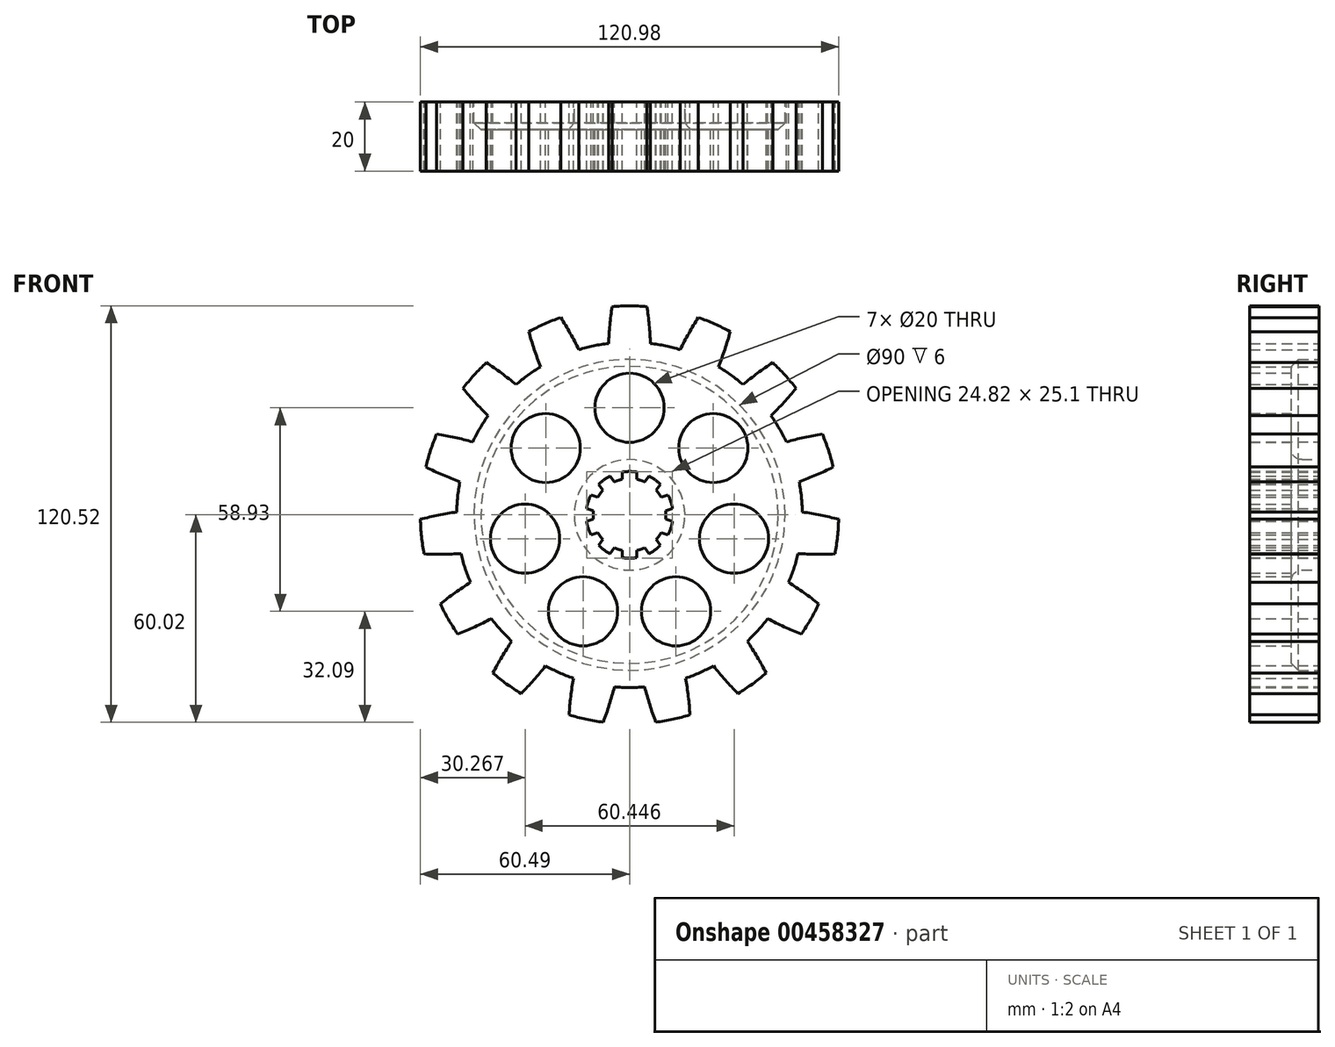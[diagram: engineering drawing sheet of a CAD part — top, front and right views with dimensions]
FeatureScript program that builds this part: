
annotation { "Feature Type Name" : "Feature", "Feature Type Description" : "" }
export const myFeature = defineFeature(function(context is Context, id is Id, definition is map)
    precondition{}
    {
        {
            var Q0;
            Q0=qCreatedBy(makeId("Front.planeOp"),FACE);
            var sketch = newSketch(context, id + "F0", { "sketchPlane" : qUnion([Q0])});
            skCircle(sketch, "E0", {"center": v(0, 0) * mm, "radius": 10.5 * mm});
            skSolve(sketch);
        }
        {
            var Q0;
            Q0=qCreatedBy(makeId("Front.planeOp"),FACE);
            var sketch = newSketch(context, id + "F1", { "sketchPlane" : qUnion([Q0])});
            skArc(sketch, "E1", {"start": v(2.05, 12.38) * mm, "mid": v(0, 12.55) * mm, "end": v(-2.05, 12.38) * mm});
            skLineSegment(sketch, "E2", {"start": v(-2.05, 6.3) * mm, "end": v(-2.05, -6.3) * mm});
            skLineSegment(sketch, "E3", {"start": v(2.05, 6.3) * mm, "end": v(2.05, -6.3) * mm});
            skLineSegment(sketch, "E4", {"start": v(2.05, -14.67) * mm, "end": v(-2.05, -14.67) * mm});
            skArc(sketch, "E5.trimOffspring", {"start": v(-2.05, -12.38) * mm, "mid": v(0, -12.55) * mm, "end": v(2.05, -12.38) * mm});
            skPoint(sketch, "E6.orphan", {"position": v(-2.05, 16.5) * mm});
            skPoint(sketch, "E7.orphan", {"position": v(2.05, 16.45) * mm});
            skLineSegment(sketch, "E8.1.0", {"start": v(-8.94, 8.81) * mm, "end": v(-7.71, 7.13) * mm});
            skArc(sketch, "E8.1.1", {"start": v(-5.62, 11.22) * mm, "mid": v(-7.38, 10.15) * mm, "end": v(-8.94, 8.81) * mm});
            skLineSegment(sketch, "E8.1.2", {"start": v(-5.62, 11.22) * mm, "end": v(-4.4, 9.54) * mm});
            skArc(sketch, "E8.1.3", {"start": v(5.62, -11.22) * mm, "mid": v(7.38, -10.15) * mm, "end": v(8.94, -8.81) * mm});
            skLineSegment(sketch, "E8.2.0", {"start": v(-12.4, 1.88) * mm, "end": v(-10.43, 1.23) * mm});
            skArc(sketch, "E8.2.1", {"start": v(-11.14, 5.78) * mm, "mid": v(-11.94, 3.88) * mm, "end": v(-12.4, 1.88) * mm});
            skLineSegment(sketch, "E8.2.2", {"start": v(-11.14, 5.78) * mm, "end": v(-9.16, 5.13) * mm});
            skArc(sketch, "E8.2.3", {"start": v(11.14, -5.78) * mm, "mid": v(11.94, -3.88) * mm, "end": v(12.4, -1.88) * mm});
            skLineSegment(sketch, "E8.3.0", {"start": v(-11.14, -5.78) * mm, "end": v(-9.16, -5.13) * mm});
            skArc(sketch, "E8.3.1", {"start": v(-12.4, -1.88) * mm, "mid": v(-11.94, -3.88) * mm, "end": v(-11.14, -5.78) * mm});
            skLineSegment(sketch, "E8.3.2", {"start": v(-12.4, -1.88) * mm, "end": v(-10.43, -1.23) * mm});
            skArc(sketch, "E8.3.3", {"start": v(12.4, 1.88) * mm, "mid": v(11.94, 3.88) * mm, "end": v(11.14, 5.78) * mm});
            skLineSegment(sketch, "E8.4.0", {"start": v(-5.62, -11.22) * mm, "end": v(-4.4, -9.54) * mm});
            skArc(sketch, "E8.4.1", {"start": v(-8.94, -8.81) * mm, "mid": v(-7.38, -10.15) * mm, "end": v(-5.62, -11.22) * mm});
            skLineSegment(sketch, "E8.4.2", {"start": v(-8.94, -8.81) * mm, "end": v(-7.71, -7.13) * mm});
            skArc(sketch, "E8.4.3", {"start": v(8.94, 8.81) * mm, "mid": v(7.38, 10.15) * mm, "end": v(5.62, 11.22) * mm});
            skLineSegment(sketch, "E8.5.0", {"start": v(2.05, -12.38) * mm, "end": v(2.05, -10.3) * mm});
            skLineSegment(sketch, "E8.5.2", {"start": v(-2.05, -12.38) * mm, "end": v(-2.05, -10.3) * mm});
            skLineSegment(sketch, "E8.6.0", {"start": v(8.94, -8.81) * mm, "end": v(7.71, -7.13) * mm});
            skArc(sketch, "E8.6.1", {"start": v(5.62, -11.22) * mm, "mid": v(7.38, -10.15) * mm, "end": v(8.94, -8.81) * mm});
            skLineSegment(sketch, "E8.6.2", {"start": v(5.62, -11.22) * mm, "end": v(4.4, -9.54) * mm});
            skArc(sketch, "E8.6.3", {"start": v(-5.62, 11.22) * mm, "mid": v(-7.38, 10.15) * mm, "end": v(-8.94, 8.81) * mm});
            skLineSegment(sketch, "E8.7.0", {"start": v(12.4, -1.88) * mm, "end": v(10.43, -1.23) * mm});
            skArc(sketch, "E8.7.1", {"start": v(11.14, -5.78) * mm, "mid": v(11.94, -3.88) * mm, "end": v(12.4, -1.88) * mm});
            skLineSegment(sketch, "E8.7.2", {"start": v(11.14, -5.78) * mm, "end": v(9.16, -5.13) * mm});
            skArc(sketch, "E8.7.3", {"start": v(-11.14, 5.78) * mm, "mid": v(-11.94, 3.88) * mm, "end": v(-12.4, 1.88) * mm});
            skLineSegment(sketch, "E8.8.0", {"start": v(11.14, 5.78) * mm, "end": v(9.16, 5.13) * mm});
            skArc(sketch, "E8.8.1", {"start": v(12.4, 1.88) * mm, "mid": v(11.94, 3.88) * mm, "end": v(11.14, 5.78) * mm});
            skLineSegment(sketch, "E8.8.2", {"start": v(12.4, 1.88) * mm, "end": v(10.43, 1.23) * mm});
            skArc(sketch, "E8.8.3", {"start": v(-12.4, -1.88) * mm, "mid": v(-11.94, -3.88) * mm, "end": v(-11.14, -5.78) * mm});
            skLineSegment(sketch, "E8.9.0", {"start": v(5.62, 11.22) * mm, "end": v(4.4, 9.54) * mm});
            skArc(sketch, "E8.9.1", {"start": v(8.94, 8.81) * mm, "mid": v(7.38, 10.15) * mm, "end": v(5.62, 11.22) * mm});
            skLineSegment(sketch, "E8.9.2", {"start": v(8.94, 8.81) * mm, "end": v(7.71, 7.13) * mm});
            skArc(sketch, "E8.9.3", {"start": v(-8.94, -8.81) * mm, "mid": v(-7.38, -10.15) * mm, "end": v(-5.62, -11.22) * mm});
            skCircle(sketch, "E9", {"center": v(0, 0) * mm, "radius": 50 * mm});
            skCircle(sketch, "E10", {"center": v(0, 0) * mm, "radius": 10.5 * mm});
            skLineSegment(sketch, "E11.trimOffspring", {"start": v(-2.05, 10.3) * mm, "end": v(-2.05, 12.38) * mm});
            skLineSegment(sketch, "E12.trimOffspring", {"start": v(-2.05, 6.3) * mm, "end": v(5.37, -3.9) * mm});
            skLineSegment(sketch, "E13.trimOffspring", {"start": v(-5.37, 3.9) * mm, "end": v(2.05, -6.3) * mm});
            skLineSegment(sketch, "E14.trimOffspring", {"start": v(-5.37, 3.9) * mm, "end": v(6.63, 0) * mm});
            skLineSegment(sketch, "E15.trimOffspring", {"start": v(-9.16, 5.13) * mm, "end": v(-11.14, 5.78) * mm});
            skLineSegment(sketch, "E16.trimOffspring", {"start": v(-6.63, 0) * mm, "end": v(5.37, -3.9) * mm});
            skLineSegment(sketch, "E17.trimOffspring", {"start": v(-10.43, -1.23) * mm, "end": v(-12.4, -1.88) * mm});
            skLineSegment(sketch, "E18.trimOffspring", {"start": v(-9.16, -5.13) * mm, "end": v(-11.14, -5.78) * mm});
            skLineSegment(sketch, "E19.trimOffspring", {"start": v(-6.63, 0) * mm, "end": v(5.37, 3.9) * mm});
            skLineSegment(sketch, "E20.trimOffspring", {"start": v(-10.43, 1.23) * mm, "end": v(-12.4, 1.88) * mm});
            skLineSegment(sketch, "E21.trimOffspring", {"start": v(-5.37, -3.9) * mm, "end": v(2.05, 6.3) * mm});
            skLineSegment(sketch, "E22.trimOffspring", {"start": v(-7.71, -7.13) * mm, "end": v(-8.94, -8.81) * mm});
            skLineSegment(sketch, "E23.trimOffspring", {"start": v(-5.37, -3.9) * mm, "end": v(6.63, 0) * mm});
            skLineSegment(sketch, "E24.trimOffspring", {"start": v(-2.05, -6.3) * mm, "end": v(5.37, 3.9) * mm});
            skLineSegment(sketch, "E25.trimOffspring", {"start": v(-2.05, -10.3) * mm, "end": v(-2.05, -12.38) * mm});
            skLineSegment(sketch, "E26.trimOffspring", {"start": v(-4.4, -9.54) * mm, "end": v(-5.62, -11.22) * mm});
            skLineSegment(sketch, "E27.trimOffspring", {"start": v(-2.05, -6.3) * mm, "end": v(-2.05, 6.3) * mm});
            skLineSegment(sketch, "E28.trimOffspring", {"start": v(2.05, -10.3) * mm, "end": v(2.05, -12.38) * mm});
            skLineSegment(sketch, "E29.trimOffspring", {"start": v(2.05, -6.3) * mm, "end": v(2.05, 2.82) * mm});
            skLineSegment(sketch, "E30.trimOffspring", {"start": v(4.4, -9.54) * mm, "end": v(5.62, -11.22) * mm});
            skLineSegment(sketch, "E31.trimOffspring", {"start": v(2.05, -6.3) * mm, "end": v(-8.94, 8.81) * mm});
            skLineSegment(sketch, "E32.trimOffspring", {"start": v(5.37, -3.9) * mm, "end": v(-2.05, 6.3) * mm});
            skLineSegment(sketch, "E33.trimOffspring", {"start": v(7.71, -7.13) * mm, "end": v(8.94, -8.81) * mm});
            skLineSegment(sketch, "E34.trimOffspring", {"start": v(9.16, -5.13) * mm, "end": v(11.14, -5.78) * mm});
            skLineSegment(sketch, "E35.trimOffspring", {"start": v(5.37, -3.9) * mm, "end": v(-6.63, 0) * mm});
            skLineSegment(sketch, "E36.trimOffspring", {"start": v(10.43, -1.23) * mm, "end": v(12.4, -1.88) * mm});
            skLineSegment(sketch, "E37.trimOffspring", {"start": v(6.63, 0) * mm, "end": v(-5.37, 3.9) * mm});
            skLineSegment(sketch, "E38.trimOffspring", {"start": v(6.63, 0) * mm, "end": v(-5.37, -3.9) * mm});
            skLineSegment(sketch, "E39.trimOffspring", {"start": v(10.43, 1.23) * mm, "end": v(12.4, 1.88) * mm});
            skLineSegment(sketch, "E40.trimOffspring", {"start": v(9.16, 5.13) * mm, "end": v(11.14, 5.78) * mm});
            skLineSegment(sketch, "E41.trimOffspring", {"start": v(5.37, 3.9) * mm, "end": v(-6.63, 0) * mm});
            skLineSegment(sketch, "E42.trimOffspring", {"start": v(7.71, 7.13) * mm, "end": v(8.94, 8.81) * mm});
            skLineSegment(sketch, "E43.trimOffspring", {"start": v(2.05, 6.3) * mm, "end": v(-5.37, -3.9) * mm});
            skLineSegment(sketch, "E44.trimOffspring", {"start": v(4.4, 9.54) * mm, "end": v(5.62, 11.22) * mm});
            skLineSegment(sketch, "E45.trimOffspring", {"start": v(5.37, 3.9) * mm, "end": v(-2.05, -6.3) * mm});
            skLineSegment(sketch, "E46.trimOffspring", {"start": v(2.05, 10.3) * mm, "end": v(2.05, 12.38) * mm});
            skSolve(sketch);
        }
        {
            var Q0;
            {var subQ6=sQuery(id+"F1.wireOp",EDGE,"E8.1.2");Q0=makeQuery(id+"F1.imprint","IMPRINT",FACE,{"disambiguationData":[TD([[makeQuery(id+"F1.imprint","IMPRINT",EDGE,{"derivedFrom":subQ6}),1.0]])]});}
            extrude(context, id + "F2", {"entities" : qUnion([Q0]), "depth" : 20 * mm, "offsetDistance" : 25 * mm});
        }
        {
            var Q0;
            Q0=qCreatedBy(makeId("Front.planeOp"),FACE);
            var sketch = newSketch(context, id + "F3", { "sketchPlane" : qUnion([Q0])});
            skArc(sketch, "E47", {"start": v(5.04, 60.29) * mm, "mid": v(0, 60.5) * mm, "end": v(-5.04, 60.29) * mm});
            skLineSegment(sketch, "E48", {"start": v(83.9, 39.47) * mm, "end": v(83.9, 58.43) * mm, "construction": true});
            skLineSegment(sketch, "E49", {"start": v(-3.15, 46.5) * mm, "end": v(91.22, 46.5) * mm, "construction": true});
            skArc(sketch, "E50", {"start": v(-5.04, 60.29) * mm, "mid": v(-5.7, 54.98) * mm, "end": v(-6.05, 49.63) * mm});
            skCircle(sketch, "E51", {"center": v(0, 0) * mm, "radius": 50 * mm});
            skArc(sketch, "E52.MirrorCS", {"start": v(5.04, 60.29) * mm, "mid": v(5.7, 54.98) * mm, "end": v(6.05, 49.63) * mm});
            skArc(sketch, "E53.1.0", {"start": v(-19.92, 57.13) * mm, "mid": v(-24.6, 55.27) * mm, "end": v(-29.12, 53.03) * mm});
            skArc(sketch, "E53.1.1", {"start": v(-29.12, 53.03) * mm, "mid": v(-27.57, 47.9) * mm, "end": v(-25.71, 42.88) * mm});
            skArc(sketch, "E53.1.2", {"start": v(-19.92, 57.13) * mm, "mid": v(-17.15, 52.54) * mm, "end": v(-14.66, 47.8) * mm});
            skArc(sketch, "E53.2.0", {"start": v(-41.43, 44.09) * mm, "mid": v(-44.96, 40.48) * mm, "end": v(-48.17, 36.6) * mm});
            skArc(sketch, "E53.2.1", {"start": v(-48.17, 36.6) * mm, "mid": v(-44.67, 32.55) * mm, "end": v(-40.93, 28.72) * mm});
            skArc(sketch, "E53.2.2", {"start": v(-41.43, 44.09) * mm, "mid": v(-37.04, 41.02) * mm, "end": v(-32.84, 37.7) * mm});
            skArc(sketch, "E53.3.0", {"start": v(-55.78, 23.42) * mm, "mid": v(-57.54, 18.7) * mm, "end": v(-58.9, 13.84) * mm});
            skArc(sketch, "E53.3.1", {"start": v(-58.9, 13.84) * mm, "mid": v(-54.05, 11.57) * mm, "end": v(-49.07, 9.59) * mm});
            skArc(sketch, "E53.3.2", {"start": v(-55.78, 23.42) * mm, "mid": v(-50.52, 22.4) * mm, "end": v(-45.34, 21.09) * mm});
            skArc(sketch, "E53.4.0", {"start": v(-60.49, -1.3) * mm, "mid": v(-60.17, -6.32) * mm, "end": v(-59.43, -11.31) * mm});
            skArc(sketch, "E53.4.1", {"start": v(-59.43, -11.31) * mm, "mid": v(-54.08, -11.42) * mm, "end": v(-48.73, -11.2) * mm});
            skArc(sketch, "E53.4.2", {"start": v(-60.49, -1.3) * mm, "mid": v(-55.27, -0.08) * mm, "end": v(-50, 0.82) * mm});
            skArc(sketch, "E53.5.0", {"start": v(-54.73, -25.78) * mm, "mid": v(-52.4, -30.25) * mm, "end": v(-49.7, -34.5) * mm});
            skArc(sketch, "E53.5.1", {"start": v(-49.7, -34.5) * mm, "mid": v(-44.76, -32.42) * mm, "end": v(-39.96, -30.05) * mm});
            skArc(sketch, "E53.5.2", {"start": v(-54.73, -25.78) * mm, "mid": v(-50.46, -22.55) * mm, "end": v(-46, -19.58) * mm});
            skArc(sketch, "E53.6.0", {"start": v(-39.51, -45.81) * mm, "mid": v(-35.56, -48.95) * mm, "end": v(-31.36, -51.74) * mm});
            skArc(sketch, "E53.6.1", {"start": v(-31.36, -51.74) * mm, "mid": v(-27.7, -47.83) * mm, "end": v(-24.28, -43.7) * mm});
            skArc(sketch, "E53.6.2", {"start": v(-39.51, -45.81) * mm, "mid": v(-36.93, -41.13) * mm, "end": v(-34.06, -36.6) * mm});
            skArc(sketch, "E53.7.0", {"start": v(-17.46, -57.93) * mm, "mid": v(-12.58, -59.18) * mm, "end": v(-7.6, -60.02) * mm});
            skArc(sketch, "E53.7.1", {"start": v(-7.6, -60.02) * mm, "mid": v(-5.85, -54.96) * mm, "end": v(-4.4, -49.8) * mm});
            skArc(sketch, "E53.7.2", {"start": v(-17.46, -57.93) * mm, "mid": v(-17, -52.6) * mm, "end": v(-16.23, -47.3) * mm});
            skArc(sketch, "E53.8.0", {"start": v(7.6, -60.02) * mm, "mid": v(12.58, -59.18) * mm, "end": v(17.46, -57.93) * mm});
            skArc(sketch, "E53.8.1", {"start": v(17.46, -57.93) * mm, "mid": v(17, -52.6) * mm, "end": v(16.23, -47.3) * mm});
            skArc(sketch, "E53.8.2", {"start": v(7.6, -60.02) * mm, "mid": v(5.85, -54.96) * mm, "end": v(4.4, -49.8) * mm});
            skArc(sketch, "E53.9.0", {"start": v(31.36, -51.74) * mm, "mid": v(35.56, -48.95) * mm, "end": v(39.51, -45.81) * mm});
            skArc(sketch, "E53.9.1", {"start": v(39.51, -45.81) * mm, "mid": v(36.93, -41.13) * mm, "end": v(34.06, -36.6) * mm});
            skArc(sketch, "E53.9.2", {"start": v(31.36, -51.74) * mm, "mid": v(27.7, -47.83) * mm, "end": v(24.28, -43.7) * mm});
            skArc(sketch, "E53.10.0", {"start": v(49.7, -34.5) * mm, "mid": v(52.4, -30.25) * mm, "end": v(54.73, -25.78) * mm});
            skArc(sketch, "E53.10.1", {"start": v(54.73, -25.78) * mm, "mid": v(50.46, -22.55) * mm, "end": v(46, -19.58) * mm});
            skArc(sketch, "E53.10.2", {"start": v(49.7, -34.5) * mm, "mid": v(44.76, -32.42) * mm, "end": v(39.96, -30.05) * mm});
            skArc(sketch, "E53.11.0", {"start": v(59.43, -11.31) * mm, "mid": v(60.17, -6.32) * mm, "end": v(60.49, -1.3) * mm});
            skArc(sketch, "E53.11.1", {"start": v(60.49, -1.3) * mm, "mid": v(55.27, -0.08) * mm, "end": v(50, 0.82) * mm});
            skArc(sketch, "E53.11.2", {"start": v(59.43, -11.31) * mm, "mid": v(54.08, -11.42) * mm, "end": v(48.73, -11.2) * mm});
            skArc(sketch, "E53.12.0", {"start": v(58.9, 13.84) * mm, "mid": v(57.54, 18.7) * mm, "end": v(55.78, 23.42) * mm});
            skArc(sketch, "E53.12.1", {"start": v(55.78, 23.42) * mm, "mid": v(50.52, 22.4) * mm, "end": v(45.34, 21.09) * mm});
            skArc(sketch, "E53.12.2", {"start": v(58.9, 13.84) * mm, "mid": v(54.05, 11.57) * mm, "end": v(49.07, 9.59) * mm});
            skArc(sketch, "E53.13.0", {"start": v(48.17, 36.6) * mm, "mid": v(44.96, 40.48) * mm, "end": v(41.43, 44.09) * mm});
            skArc(sketch, "E53.13.1", {"start": v(41.43, 44.09) * mm, "mid": v(37.04, 41.02) * mm, "end": v(32.84, 37.7) * mm});
            skArc(sketch, "E53.13.2", {"start": v(48.17, 36.6) * mm, "mid": v(44.67, 32.55) * mm, "end": v(40.93, 28.72) * mm});
            skArc(sketch, "E53.14.0", {"start": v(29.12, 53.03) * mm, "mid": v(24.6, 55.27) * mm, "end": v(19.92, 57.13) * mm});
            skArc(sketch, "E53.14.1", {"start": v(19.92, 57.13) * mm, "mid": v(17.15, 52.54) * mm, "end": v(14.66, 47.8) * mm});
            skArc(sketch, "E53.14.2", {"start": v(29.12, 53.03) * mm, "mid": v(27.57, 47.9) * mm, "end": v(25.71, 42.88) * mm});
            skSolve(sketch);
        }
        {
            var Q0;
            Q0=makeQuery(id+"F3.imprint","IMPRINT",FACE,{"disambiguationData":[TD([[makeQuery(id+"F3.imprint","IMPRINT",EDGE,{"derivedFrom":sQuery(id+"F3.wireOp",EDGE,"E47")}),1.0]])]});
            var Q1;
            Q1=makeQuery(id+"F3.imprint","IMPRINT",FACE,{"disambiguationData":[TD([[makeQuery(id+"F3.imprint","IMPRINT",EDGE,{"derivedFrom":sQuery(id+"F3.wireOp",EDGE,"E53.14.0")}),1.0]])]});
            var Q2;
            Q2=makeQuery(id+"F3.imprint","IMPRINT",FACE,{"disambiguationData":[TD([[makeQuery(id+"F3.imprint","IMPRINT",EDGE,{"derivedFrom":sQuery(id+"F3.wireOp",EDGE,"E53.13.0")}),1.0]])]});
            var Q3;
            Q3=makeQuery(id+"F3.imprint","IMPRINT",FACE,{"disambiguationData":[TD([[makeQuery(id+"F3.imprint","IMPRINT",EDGE,{"derivedFrom":sQuery(id+"F3.wireOp",EDGE,"E53.12.0")}),1.0]])]});
            var Q4;
            Q4=makeQuery(id+"F3.imprint","IMPRINT",FACE,{"disambiguationData":[TD([[makeQuery(id+"F3.imprint","IMPRINT",EDGE,{"derivedFrom":sQuery(id+"F3.wireOp",EDGE,"E53.11.0")}),1.0]])]});
            var Q5;
            Q5=makeQuery(id+"F3.imprint","IMPRINT",FACE,{"disambiguationData":[TD([[makeQuery(id+"F3.imprint","IMPRINT",EDGE,{"derivedFrom":sQuery(id+"F3.wireOp",EDGE,"E53.10.0")}),1.0]])]});
            var Q6;
            Q6=makeQuery(id+"F3.imprint","IMPRINT",FACE,{"disambiguationData":[TD([[makeQuery(id+"F3.imprint","IMPRINT",EDGE,{"derivedFrom":sQuery(id+"F3.wireOp",EDGE,"E53.9.0")}),1.0]])]});
            var Q7;
            Q7=makeQuery(id+"F3.imprint","IMPRINT",FACE,{"disambiguationData":[TD([[makeQuery(id+"F3.imprint","IMPRINT",EDGE,{"derivedFrom":sQuery(id+"F3.wireOp",EDGE,"E53.8.0")}),1.0]])]});
            var Q8;
            Q8=makeQuery(id+"F3.imprint","IMPRINT",FACE,{"disambiguationData":[TD([[makeQuery(id+"F3.imprint","IMPRINT",EDGE,{"derivedFrom":sQuery(id+"F3.wireOp",EDGE,"E53.7.0")}),1.0]])]});
            var Q9;
            Q9=makeQuery(id+"F3.imprint","IMPRINT",FACE,{"disambiguationData":[TD([[makeQuery(id+"F3.imprint","IMPRINT",EDGE,{"derivedFrom":sQuery(id+"F3.wireOp",EDGE,"E53.6.0")}),1.0]])]});
            var Q10;
            Q10=makeQuery(id+"F3.imprint","IMPRINT",FACE,{"disambiguationData":[TD([[makeQuery(id+"F3.imprint","IMPRINT",EDGE,{"derivedFrom":sQuery(id+"F3.wireOp",EDGE,"E53.5.0")}),1.0]])]});
            var Q11;
            Q11=makeQuery(id+"F3.imprint","IMPRINT",FACE,{"disambiguationData":[TD([[makeQuery(id+"F3.imprint","IMPRINT",EDGE,{"derivedFrom":sQuery(id+"F3.wireOp",EDGE,"E53.4.0")}),1.0]])]});
            var Q12;
            Q12=makeQuery(id+"F3.imprint","IMPRINT",FACE,{"disambiguationData":[TD([[makeQuery(id+"F3.imprint","IMPRINT",EDGE,{"derivedFrom":sQuery(id+"F3.wireOp",EDGE,"E53.3.0")}),1.0]])]});
            var Q13;
            Q13=makeQuery(id+"F3.imprint","IMPRINT",FACE,{"disambiguationData":[TD([[makeQuery(id+"F3.imprint","IMPRINT",EDGE,{"derivedFrom":sQuery(id+"F3.wireOp",EDGE,"E53.2.0")}),1.0]])]});
            var Q14;
            Q14=makeQuery(id+"F3.imprint","IMPRINT",FACE,{"disambiguationData":[TD([[makeQuery(id+"F3.imprint","IMPRINT",EDGE,{"derivedFrom":sQuery(id+"F3.wireOp",EDGE,"E53.1.0")}),1.0]])]});
            extrude(context, id + "F4", {"entities" : qUnion([Q0, Q1, Q2, Q3, Q4, Q5, Q6, Q7, Q8, Q9, Q10, Q11, Q12, Q13, Q14]), "operationType" : NewBodyOperationType.ADD, "depth" : 20 * mm, "offsetDistance" : 25 * mm});
        }
        {
            var Q0;
            Q0=qCreatedBy(makeId("Front.planeOp"),FACE);
            var sketch = newSketch(context, id + "F5", { "sketchPlane" : qUnion([Q0])});
            skCircle(sketch, "E54", {"center": v(0, 0) * mm, "radius": 45 * mm});
            skCircle(sketch, "E55", {"center": v(0, 0) * mm, "radius": 16 * mm});
            skSolve(sketch);
        }
        {
            var Q0;
            Q0=makeQuery(id+"F5.imprint","IMPRINT",FACE,{"disambiguationData":[TD([[makeQuery(id+"F5.imprint","IMPRINT",EDGE,{"derivedFrom":sQuery(id+"F5.wireOp",EDGE,"E54")}),1.0]])]});
            extrude(context, id + "F6", {"entities" : qUnion([Q0]), "operationType" : NewBodyOperationType.REMOVE, "depth" : 8 * mm, "offsetDistance" : 25 * mm});
        }
        {
            var Q0;
            Q0=qCreatedBy(makeId("Front.planeOp"),FACE);
            var sketch = newSketch(context, id + "F7", { "sketchPlane" : qUnion([Q0])});
            skCircle(sketch, "E56", {"center": v(0, 31) * mm, "radius": 10 * mm});
            skCircle(sketch, "E57.1.0", {"center": v(-24.24, 19.33) * mm, "radius": 10 * mm});
            skCircle(sketch, "E57.2.0", {"center": v(-30.22, -6.9) * mm, "radius": 10 * mm});
            skCircle(sketch, "E57.3.0", {"center": v(-13.45, -27.93) * mm, "radius": 10 * mm});
            skCircle(sketch, "E57.4.0", {"center": v(13.45, -27.93) * mm, "radius": 10 * mm});
            skCircle(sketch, "E57.5.0", {"center": v(30.22, -6.9) * mm, "radius": 10 * mm});
            skCircle(sketch, "E57.6.0", {"center": v(24.24, 19.33) * mm, "radius": 10 * mm});
            skPoint(sketch, "E57.center", {"position": v(0, 0) * mm});
            skSolve(sketch);
        }
        {
            var Q0;
            Q0=makeQuery(id+"F7.imprint","IMPRINT",FACE,{"disambiguationData":[TD([[makeQuery(id+"F7.imprint","IMPRINT",EDGE,{"derivedFrom":sQuery(id+"F7.wireOp",EDGE,"E56")}),1.0]])]});
            var Q1;
            Q1=makeQuery(id+"F7.imprint","IMPRINT",FACE,{"disambiguationData":[TD([[makeQuery(id+"F7.imprint","IMPRINT",EDGE,{"derivedFrom":sQuery(id+"F7.wireOp",EDGE,"E57.1.0")}),1.0]])]});
            var Q2;
            Q2=makeQuery(id+"F7.imprint","IMPRINT",FACE,{"disambiguationData":[TD([[makeQuery(id+"F7.imprint","IMPRINT",EDGE,{"derivedFrom":sQuery(id+"F7.wireOp",EDGE,"E57.2.0")}),1.0]])]});
            var Q3;
            Q3=makeQuery(id+"F7.imprint","IMPRINT",FACE,{"disambiguationData":[TD([[makeQuery(id+"F7.imprint","IMPRINT",EDGE,{"derivedFrom":sQuery(id+"F7.wireOp",EDGE,"E57.3.0")}),1.0]])]});
            var Q4;
            Q4=makeQuery(id+"F7.imprint","IMPRINT",FACE,{"disambiguationData":[TD([[makeQuery(id+"F7.imprint","IMPRINT",EDGE,{"derivedFrom":sQuery(id+"F7.wireOp",EDGE,"E57.4.0")}),1.0]])]});
            var Q5;
            Q5=makeQuery(id+"F7.imprint","IMPRINT",FACE,{"disambiguationData":[TD([[makeQuery(id+"F7.imprint","IMPRINT",EDGE,{"derivedFrom":sQuery(id+"F7.wireOp",EDGE,"E57.5.0")}),1.0]])]});
            var Q6;
            Q6=makeQuery(id+"F7.imprint","IMPRINT",FACE,{"disambiguationData":[TD([[makeQuery(id+"F7.imprint","IMPRINT",EDGE,{"derivedFrom":sQuery(id+"F7.wireOp",EDGE,"E57.6.0")}),1.0]])]});
            extrude(context, id + "F8", {"entities" : qUnion([Q0, Q1, Q2, Q3, Q4, Q5, Q6]), "operationType" : NewBodyOperationType.REMOVE, "depth" : 25 * mm, "offsetDistance" : 25 * mm});
        }
        {
            var Q0;
            Q0=makeQuery(id+"F6.boolean.opBoolean","COPY",EDGE,{"derivedFrom":makeQuery(id+"F6.opExtrude","CAP_EDGE",EDGE,{"disambiguationData":[OSD([sQuery(id+"F5.wireOp",EDGE,"E54")])],"isStart":true})});
            var Q1;
            Q1=makeQuery(id+"F6.boolean.opBoolean","COPY",EDGE,{"derivedFrom":makeQuery(id+"F6.opExtrude","CAP_EDGE",EDGE,{"disambiguationData":[OSD([sQuery(id+"F5.wireOp",EDGE,"E54")])],"isStart":false})});
            chamfer(context, id + "F9", {"entities" : qUnion([Q0, Q1]), "width" : 2 * mm, "tangentPropagation" : true});
        }
        {
            var Q0;
            Q0=makeQuery(id+"F6.boolean.opBoolean","COPY",EDGE,{"derivedFrom":makeQuery(id+"F6.opExtrude","CAP_EDGE",EDGE,{"disambiguationData":[OSD([sQuery(id+"F5.wireOp",EDGE,"E55")])],"isStart":false})});
            fillet(context, id + "F10", {"entities" : qUnion([Q0]), "radius" : 3 * mm, "tangentPropagation" : true, "allowEdgeOverflow" : false});
        }
    });
